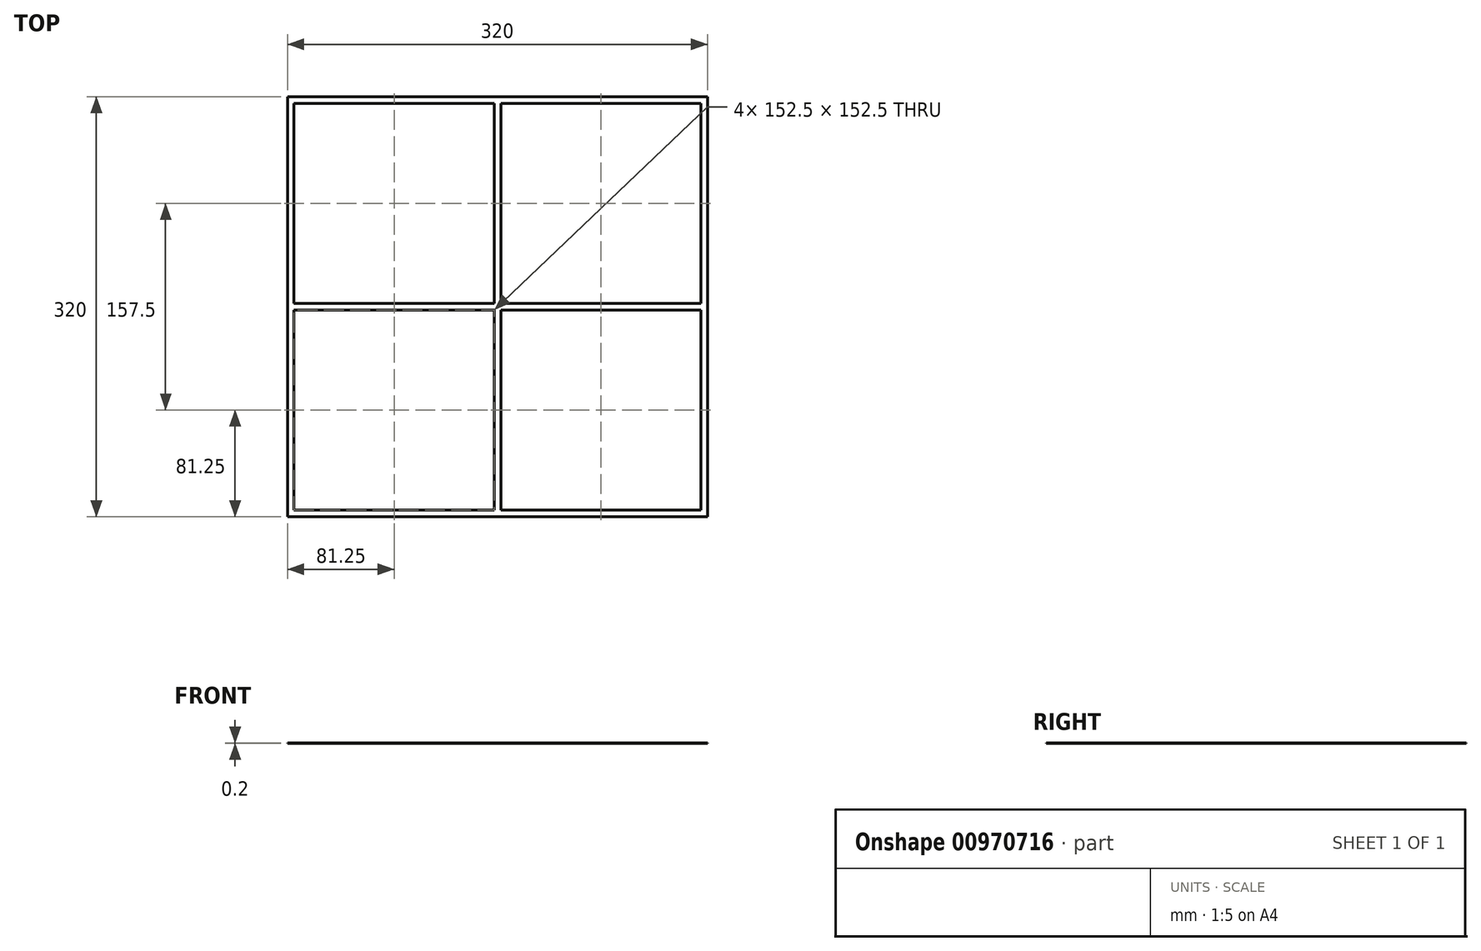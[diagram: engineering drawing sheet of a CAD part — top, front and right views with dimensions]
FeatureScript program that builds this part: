
annotation { "Feature Type Name" : "Feature", "Feature Type Description" : "" }
export const myFeature = defineFeature(function(context is Context, id is Id, definition is map)
    precondition{}
    {
        {
            var Q0;
            Q0=qCreatedBy(makeId("Top.planeOp"),FACE);
            var sketch = newSketch(context, id + "F0", { "sketchPlane" : qUnion([Q0])});
            skLineSegment(sketch, "E0.bottom", {"start": v(160, -160) * mm, "end": v(-160, -160) * mm});
            skLineSegment(sketch, "E0.top", {"start": v(160, 160) * mm, "end": v(-160, 160) * mm});
            skLineSegment(sketch, "E0.left", {"start": v(160, -160) * mm, "end": v(160, 160) * mm});
            skLineSegment(sketch, "E0.right", {"start": v(-160, -160) * mm, "end": v(-160, 160) * mm});
            skPoint(sketch, "E0.middle", {"position": v(0, 0) * mm});
            skLineSegment(sketch, "E1.0", {"start": v(155, 155) * mm, "end": v(2.5, 155) * mm});
            skLineSegment(sketch, "E1.1", {"start": v(155, -155) * mm, "end": v(155, -2.5) * mm});
            skLineSegment(sketch, "E1.2", {"start": v(155, -155) * mm, "end": v(2.5, -155) * mm});
            skLineSegment(sketch, "E1.3", {"start": v(-155, -155) * mm, "end": v(-155, -2.5) * mm});
            skLineSegment(sketch, "E2", {"start": v(0, 155) * mm, "end": v(0, -155) * mm, "construction": true});
            skLineSegment(sketch, "E3", {"start": v(155, 0) * mm, "end": v(-155, 0) * mm, "construction": true});
            skLineSegment(sketch, "E4.0", {"start": v(-2.5, 155) * mm, "end": v(-2.5, 2.5) * mm});
            skLineSegment(sketch, "E5.0", {"start": v(155, 2.5) * mm, "end": v(2.5, 2.5) * mm});
            skLineSegment(sketch, "E6.MirrorCS", {"start": v(2.5, 155) * mm, "end": v(2.5, 2.5) * mm});
            skLineSegment(sketch, "E7.MirrorCS", {"start": v(155, -2.5) * mm, "end": v(2.5, -2.5) * mm});
            skLineSegment(sketch, "E8.trimOffspring", {"start": v(-2.5, 155) * mm, "end": v(-155, 155) * mm});
            skLineSegment(sketch, "E9.trimOffspring", {"start": v(-155, 2.5) * mm, "end": v(-155, 155) * mm});
            skLineSegment(sketch, "E10.trimOffspring", {"start": v(155, 2.5) * mm, "end": v(155, 155) * mm});
            skLineSegment(sketch, "E11.trimOffspring", {"start": v(-2.5, -155) * mm, "end": v(-155, -155) * mm});
            skLineSegment(sketch, "E12.trimOffspring", {"start": v(-2.5, 2.5) * mm, "end": v(-155, 2.5) * mm});
            skLineSegment(sketch, "E13.trimOffspring", {"start": v(-2.5, -2.5) * mm, "end": v(-2.5, -155) * mm});
            skLineSegment(sketch, "E14.trimOffspring", {"start": v(-2.5, -2.5) * mm, "end": v(-155, -2.5) * mm});
            skLineSegment(sketch, "E15.trimOffspring", {"start": v(2.5, -2.5) * mm, "end": v(2.5, -155) * mm});
            skSolve(sketch);
        }
        {
            var Q0;
            Q0=makeQuery(id+"F0.imprint","IMPRINT",FACE,{"disambiguationData":[TD([[makeQuery(id+"F0.imprint","IMPRINT",EDGE,{"derivedFrom":sQuery(id+"F0.wireOp",EDGE,"E0.bottom")}),-1.0]])]});
            extrude(context, id + "F1", {"entities" : qUnion([Q0]), "depth" : 0.2 * mm, "offsetDistance" : 25 * mm});
        }
    });
